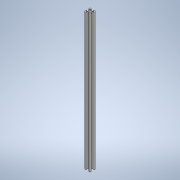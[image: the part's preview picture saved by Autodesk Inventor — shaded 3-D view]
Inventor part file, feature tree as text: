
AUTODESK INVENTOR PART (.ipt)
format: ipt  version: 2021 (Build 250183000, 183)  size: 620,032 bytes
history: native  units: mm
features: sketch x7, hole x4, extrude x3, fillet x2, projected_geometry x2, other x1, pattern_circular x1, pattern_linear x1
ambient origin geometry x8: Origin, YZ Plane, XZ Plane, XY Plane, X Axis, Y Axis, Z Axis, Center Point
bodies: Body1 (feature_tree)
feature tree (21):
  other  "實體1"
  extrude  "擠出1"  Depth=20.0mm
  extrude  "擠出2"  Depth=20.0mm
  fillet  "圓角1"  Radius=335.0mm
  pattern_circular  "環形陣列1"  [2 undecoded]
  hole  "孔1"  [1 undecoded]
  fillet  "圓角2"  Radius=6.2mm
  hole  "孔2"  [1 undecoded]
  hole  "孔3"  [1 undecoded]
  pattern_linear  "矩形陣列1"  Spacing1=1.5mm  [1 undecoded]
  extrude  "擠出3"  Depth=8.0mm
  hole  "孔4"  [1 undecoded]
  sketch  "草圖1"
  sketch  "草圖2"
  projected_geometry  "投影迴路1"
  sketch  "草圖3"
  sketch  "草圖4"
  sketch  "草圖5"
  sketch  "草圖6"
  projected_geometry  "投影迴路2"
  sketch  "草圖7"
note: 7 required parameter values undecoded (feature->parameter linkage not recoverable at this tier; creation-order binding heuristic only, values carry confidence <= 0.55)
